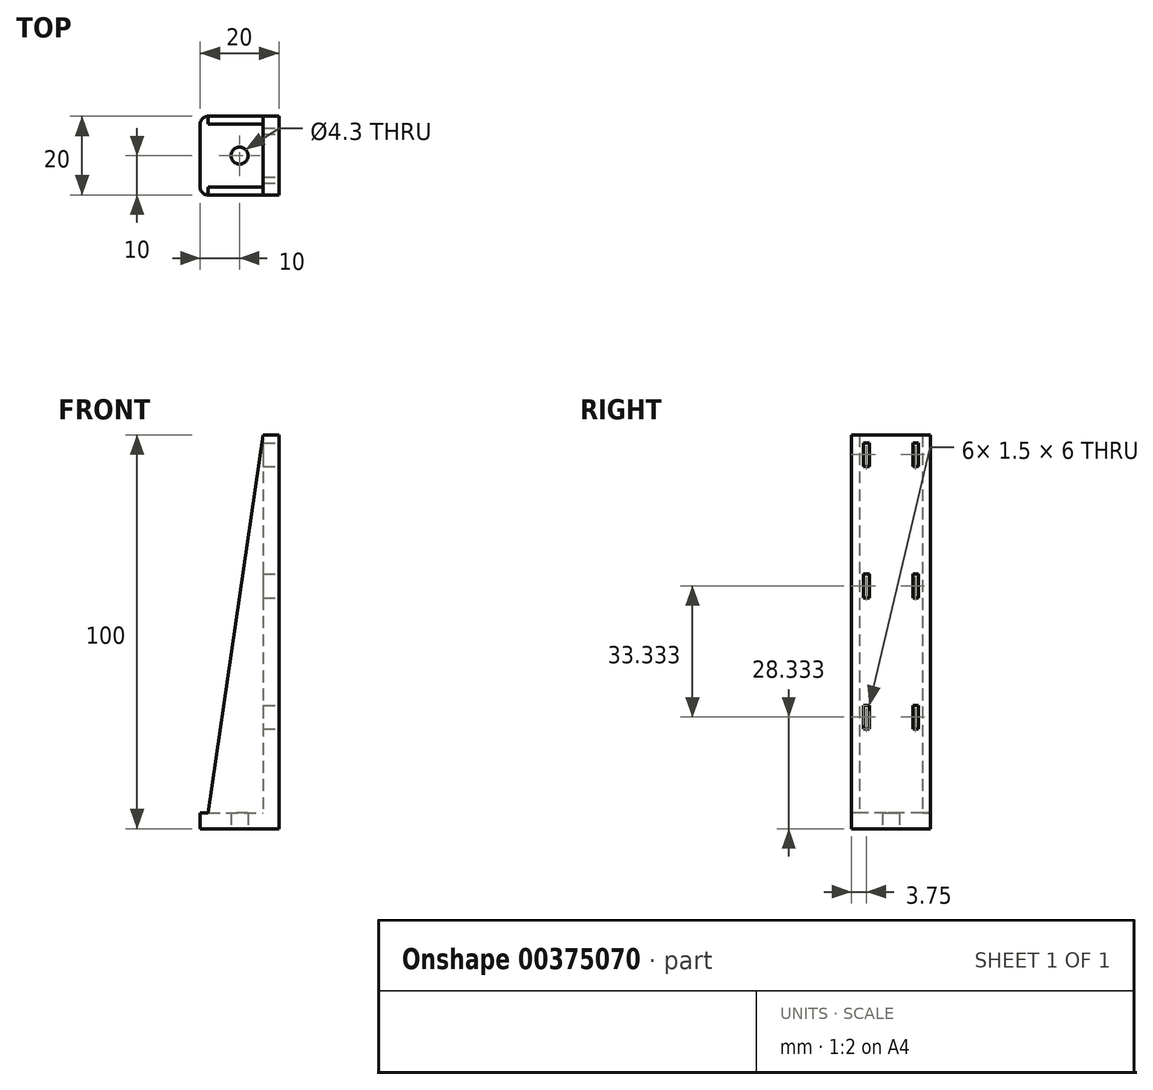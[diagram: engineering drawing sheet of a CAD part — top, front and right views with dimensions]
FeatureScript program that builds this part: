
annotation { "Feature Type Name" : "Feature", "Feature Type Description" : "" }
export const myFeature = defineFeature(function(context is Context, id is Id, definition is map)
    precondition{}
    {
        {
            var Q0;
            Q0=qCreatedBy(makeId("Top.planeOp"),FACE);
            var sketch = newSketch(context, id + "F0", { "sketchPlane" : qUnion([Q0])});
            skLineSegment(sketch, "E0.bottom", {"start": v(0, 0) * mm, "end": v(20, 0) * mm});
            skLineSegment(sketch, "E0.top", {"start": v(0, 20) * mm, "end": v(20, 20) * mm});
            skLineSegment(sketch, "E0.left", {"start": v(0, 0) * mm, "end": v(0, 20) * mm});
            skLineSegment(sketch, "E0.right", {"start": v(20, 0) * mm, "end": v(20, 20) * mm});
            skCircle(sketch, "E1", {"center": v(10, 10) * mm, "radius": 2.15 * mm});
            skPoint(sketch, "E1.centerSnap0", {"position": v(20, 10) * mm});
            skPoint(sketch, "E1.centerSnap1", {"position": v(10, 20) * mm});
            skSolve(sketch);
        }
        {
            var Q0;
            Q0=makeQuery(id+"F0.imprint","IMPRINT",FACE,{"disambiguationData":[TD([[makeQuery(id+"F0.imprint","IMPRINT",EDGE,{"derivedFrom":sQuery(id+"F0.wireOp",EDGE,"E0.bottom")}),1.0]])]});
            extrude(context, id + "F1", {"entities" : qUnion([Q0]), "depth" : 4 * mm});
        }
        {
            var Q0;
            Q0=makeQuery(id+"F1.opExtrude","CAP_FACE",FACE,{"disambiguationData":[OSD([sQuery(id+"F0.wireOp",EDGE,"E0.bottom"),sQuery(id+"F0.wireOp",EDGE,"E0.top"),sQuery(id+"F0.wireOp",EDGE,"E0.left"),sQuery(id+"F0.wireOp",EDGE,"E0.right"),sQuery(id+"F0.wireOp",EDGE,"E1")])],"isStart":false});
            var sketch = newSketch(context, id + "F2", { "sketchPlane" : qUnion([Q0])});
            skLineSegment(sketch, "E2.bottom", {"start": v(20, 20) * mm, "end": v(16, 20) * mm});
            skLineSegment(sketch, "E2.top", {"start": v(20, 0) * mm, "end": v(16, 0) * mm});
            skLineSegment(sketch, "E2.left", {"start": v(20, 20) * mm, "end": v(20, 0) * mm});
            skLineSegment(sketch, "E2.right", {"start": v(16, 20) * mm, "end": v(16, 0) * mm});
            skSolve(sketch);
        }
        {
            var Q0;
            Q0=makeQuery(id+"F2.imprint","IMPRINT",FACE,{"disambiguationData":[TD([[makeQuery(id+"F2.imprint","IMPRINT",EDGE,{"derivedFrom":sQuery(id+"F2.wireOp",EDGE,"E2.bottom")}),-1.0]])]});
            extrude(context, id + "F3", {"entities" : qUnion([Q0]), "operationType" : NewBodyOperationType.ADD, "depth" : (100 - 4) * mm});
        }
        {
            var Q0;
            Q0=makeQuery(id+"F3.boolean.opBoolean","MERGE",FACE,{"derivedFrom":[makeQuery(id+"F1.opExtrude","SWEPT_FACE",FACE,{"disambiguationData":[OSD([sQuery(id+"F0.wireOp",EDGE,"E0.right")])]}),makeQuery(id+"F3.opExtrude","SWEPT_FACE",FACE,{"disambiguationData":[OSD([sQuery(id+"F2.wireOp",EDGE,"E2.left")])]})]});
            var sketch = newSketch(context, id + "F4", { "sketchPlane" : qUnion([Q0])});
            skLineSegment(sketch, "E3.bottom", {"start": v(3, 98) * mm, "end": v(4.5, 98) * mm});
            skLineSegment(sketch, "E3.top", {"start": v(3, 92) * mm, "end": v(4.5, 92) * mm});
            skLineSegment(sketch, "E3.left", {"start": v(3, 98) * mm, "end": v(3, 92) * mm});
            skLineSegment(sketch, "E3.right", {"start": v(4.5, 98) * mm, "end": v(4.5, 92) * mm});
            skLineSegment(sketch, "E4.bottom", {"start": v(15.5, 98) * mm, "end": v(17, 98) * mm});
            skLineSegment(sketch, "E4.top", {"start": v(15.5, 92) * mm, "end": v(17, 92) * mm});
            skLineSegment(sketch, "E4.left", {"start": v(15.5, 98) * mm, "end": v(15.5, 92) * mm});
            skLineSegment(sketch, "E4.right", {"start": v(17, 98) * mm, "end": v(17, 92) * mm});
            skLineSegment(sketch, "E5.1.0.0", {"start": v(3, 64.67) * mm, "end": v(4.5, 64.67) * mm});
            skLineSegment(sketch, "E5.1.0.1", {"start": v(3, 64.67) * mm, "end": v(3, 58.67) * mm});
            skLineSegment(sketch, "E5.1.0.2", {"start": v(3, 58.67) * mm, "end": v(4.5, 58.67) * mm});
            skLineSegment(sketch, "E5.1.0.3", {"start": v(4.5, 64.67) * mm, "end": v(4.5, 58.67) * mm});
            skLineSegment(sketch, "E5.1.0.4", {"start": v(15.5, 58.67) * mm, "end": v(17, 58.67) * mm});
            skLineSegment(sketch, "E5.1.0.5", {"start": v(15.5, 64.67) * mm, "end": v(15.5, 58.67) * mm});
            skLineSegment(sketch, "E5.1.0.6", {"start": v(17, 64.67) * mm, "end": v(17, 58.67) * mm});
            skLineSegment(sketch, "E5.1.0.7", {"start": v(15.5, 64.67) * mm, "end": v(17, 64.67) * mm});
            skLineSegment(sketch, "E5.2.0.0", {"start": v(3, 31.33) * mm, "end": v(4.5, 31.33) * mm});
            skLineSegment(sketch, "E5.2.0.1", {"start": v(3, 31.33) * mm, "end": v(3, 25.33) * mm});
            skLineSegment(sketch, "E5.2.0.2", {"start": v(3, 25.33) * mm, "end": v(4.5, 25.33) * mm});
            skLineSegment(sketch, "E5.2.0.3", {"start": v(4.5, 31.33) * mm, "end": v(4.5, 25.33) * mm});
            skLineSegment(sketch, "E5.2.0.4", {"start": v(15.5, 25.33) * mm, "end": v(17, 25.33) * mm});
            skLineSegment(sketch, "E5.2.0.5", {"start": v(15.5, 31.33) * mm, "end": v(15.5, 25.33) * mm});
            skLineSegment(sketch, "E5.2.0.6", {"start": v(17, 31.33) * mm, "end": v(17, 25.33) * mm});
            skLineSegment(sketch, "E5.2.0.7", {"start": v(15.5, 31.33) * mm, "end": v(17, 31.33) * mm});
            skLineSegment(sketch, "E5.direction1", {"start": v(3, 92) * mm, "end": v(3, 58.67) * mm, "construction": true});
            skSolve(sketch);
        }
        {
            var Q0;
            Q0=qSketchRegion(id+"F4",true);
            extrude(context, id + "F5", {"entities" : qUnion([Q0]), "operationType" : NewBodyOperationType.REMOVE, "endBound" : BoundingType.THROUGH_ALL, "oppositeDirection" : true, "depth" : 25 * mm});
        }
        {
            var Q0;
            Q0=makeQuery(id+"F1.opExtrude","SWEPT_EDGE",EDGE,{"disambiguationData":[OSD([sQuery(id+"F0.wireOp",EDGE,"E0.bottom"),sQuery(id+"F0.wireOp",EDGE,"E0.left")])]});
            var Q1;
            Q1=makeQuery(id+"F1.opExtrude","SWEPT_EDGE",EDGE,{"disambiguationData":[OSD([sQuery(id+"F0.wireOp",EDGE,"E0.top"),sQuery(id+"F0.wireOp",EDGE,"E0.left")])]});
            fillet(context, id + "F6", {"entities" : qUnion([Q0, Q1]), "radius" : 2 * mm, "tangentPropagation" : true, "allowEdgeOverflow" : false});
        }
        {
            var Q0;
            Q0=makeQuery(id+"F3.boolean.opBoolean","MERGE",FACE,{"derivedFrom":[makeQuery(id+"F1.opExtrude","SWEPT_FACE",FACE,{"disambiguationData":[OSD([sQuery(id+"F0.wireOp",EDGE,"E0.bottom")])]}),makeQuery(id+"F3.opExtrude","SWEPT_FACE",FACE,{"disambiguationData":[OSD([sQuery(id+"F2.wireOp",EDGE,"E2.top")])]})]});
            var sketch = newSketch(context, id + "F7", { "sketchPlane" : qUnion([Q0])});
            skLineSegment(sketch, "E6", {"start": v(16, 100) * mm, "end": v(2, 4) * mm});
            skSolve(sketch);
        }
        {
            var Q0;
            Q0=makeQuery(id+"F7.imprint","IMPRINT",FACE,{"disambiguationData":[TD([[makeQuery(id+"F7.imprint","IMPRINT",EDGE,{"derivedFrom":sQuery(id+"F7.wireOp",EDGE,"E6")}),1.0]])]});
            extrude(context, id + "F8", {"entities" : qUnion([Q0]), "operationType" : NewBodyOperationType.ADD, "oppositeDirection" : true, "depth" : 2 * mm});
        }
        {
            var Q0;
            Q0=makeQuery(id+"F3.boolean.opBoolean","MERGE",FACE,{"derivedFrom":[makeQuery(id+"F1.opExtrude","SWEPT_FACE",FACE,{"disambiguationData":[OSD([sQuery(id+"F0.wireOp",EDGE,"E0.top")])]}),makeQuery(id+"F3.opExtrude","SWEPT_FACE",FACE,{"disambiguationData":[OSD([sQuery(id+"F2.wireOp",EDGE,"E2.bottom")])]})]});
            var sketch = newSketch(context, id + "F9", { "sketchPlane" : qUnion([Q0])});
            skLineSegment(sketch, "E7", {"start": v(-2, 4) * mm, "end": v(-16, 100) * mm});
            skSolve(sketch);
        }
        {
            var Q0;
            Q0=makeQuery(id+"F9.imprint","IMPRINT",FACE,{"disambiguationData":[TD([[makeQuery(id+"F9.imprint","IMPRINT",EDGE,{"derivedFrom":sQuery(id+"F9.wireOp",EDGE,"E7")}),1.0]])]});
            extrude(context, id + "F10", {"entities" : qUnion([Q0]), "operationType" : NewBodyOperationType.ADD, "oppositeDirection" : true, "depth" : 2 * mm});
        }
    });
